# Revit family: FP-Revit19-en-RS6009V2RT1-RS6009V2R1-RS6009SBLT1-RS6009SBL1-IntegratedRefrigerator-0-90003378B-NZ-AU-UK-IE-EU-CN-ASIA-SG
name_source: partatom
category: Specialty Equipment
units: mm (PartAtom-declared; Revit-internal decimal feet)

## family parameters
Always vertical = Yes
Cut with Voids When Loaded = Yes
OmniClass Number = 23.40.40.11.11
OmniClass Title = Refrigerators and Freezers
Part Type = Normal
Room Calculation Point = No
Round Connector Dimension = Use Diameter
Shared = No
Work Plane-Based = No

## types (8) — shared parameters
Cavity - Depth (600mm min with services external) = 600 mm  [stored 1.9685 ft]
Cavity - Width = 600 mm  [stored 1.9685 ft]
Connector Description - Electrical = 230 V, 50 Hz, 10 A circuit
Manufacturer = Fisher & Paykel Appliances
Material - Body = Fisher & Paykel - Grey
Material - Door Structure = Fisher & Paykel - White
Panel - Height = 771 mm  [stored 2.52953 ft]
Product - Depth (exl front panel) = 579 mm  [stored 1.89961 ft]
Product - Width = 592 mm  [stored 1.94226 ft]
URL = www.fisherpaykel.com
zero-valued in all types: Default Elevation

## per-type parameters (varying)
| type | Description | Handle Offset | Model |
| RS6009V2RT1 - Stainless Steel Panel | 60cm Integrated Wine Cabinet | 529 mm  [stored 1.73556 ft] | RS6009V2RT1 |
| RS6009SBL1- Stainless Steel Panel | 60cm Integrated Beverage Centre | 63 mm | RS6009SBL1 |
| RS6009V2R1 - Stainless Steel Panel | 60cm Integrated Wine Cabinet | 529 mm  [stored 1.73556 ft] | RS6009V2R1 |
| RS6009SBLT1 - Stainless Steel Panel | 60cm Integrated Beverage Centre | 63 mm | RS6009SBLT1 |
| RS6009SBL1- Custom Door Panel | 60cm Integrated Beverage Centre | 63 mm | RS6009SBL1 |
| RS6009SBLT1 - Custom Door Panel | 60cm Integrated Beverage Centre | 63 mm | RS6009SBLT1 |
| RS6009V2R1 - Custom Door Panel | 60cm Integrated Wine Cabinet | 529 mm  [stored 1.73556 ft] | RS6009V2R1 |
| RS6009V2RT1 - Custom Door Panel | 60cm Integrated Wine Cabinet | 529 mm  [stored 1.73556 ft] | RS6009V2RT1 |

note: [stored X ft] marks values corroborated as IEEE doubles in the binary element streams (Revit-internal decimal feet)

## geometry (parser evidence)
native form markers: Sweep x14
no freeform markers — native parametric forms only
